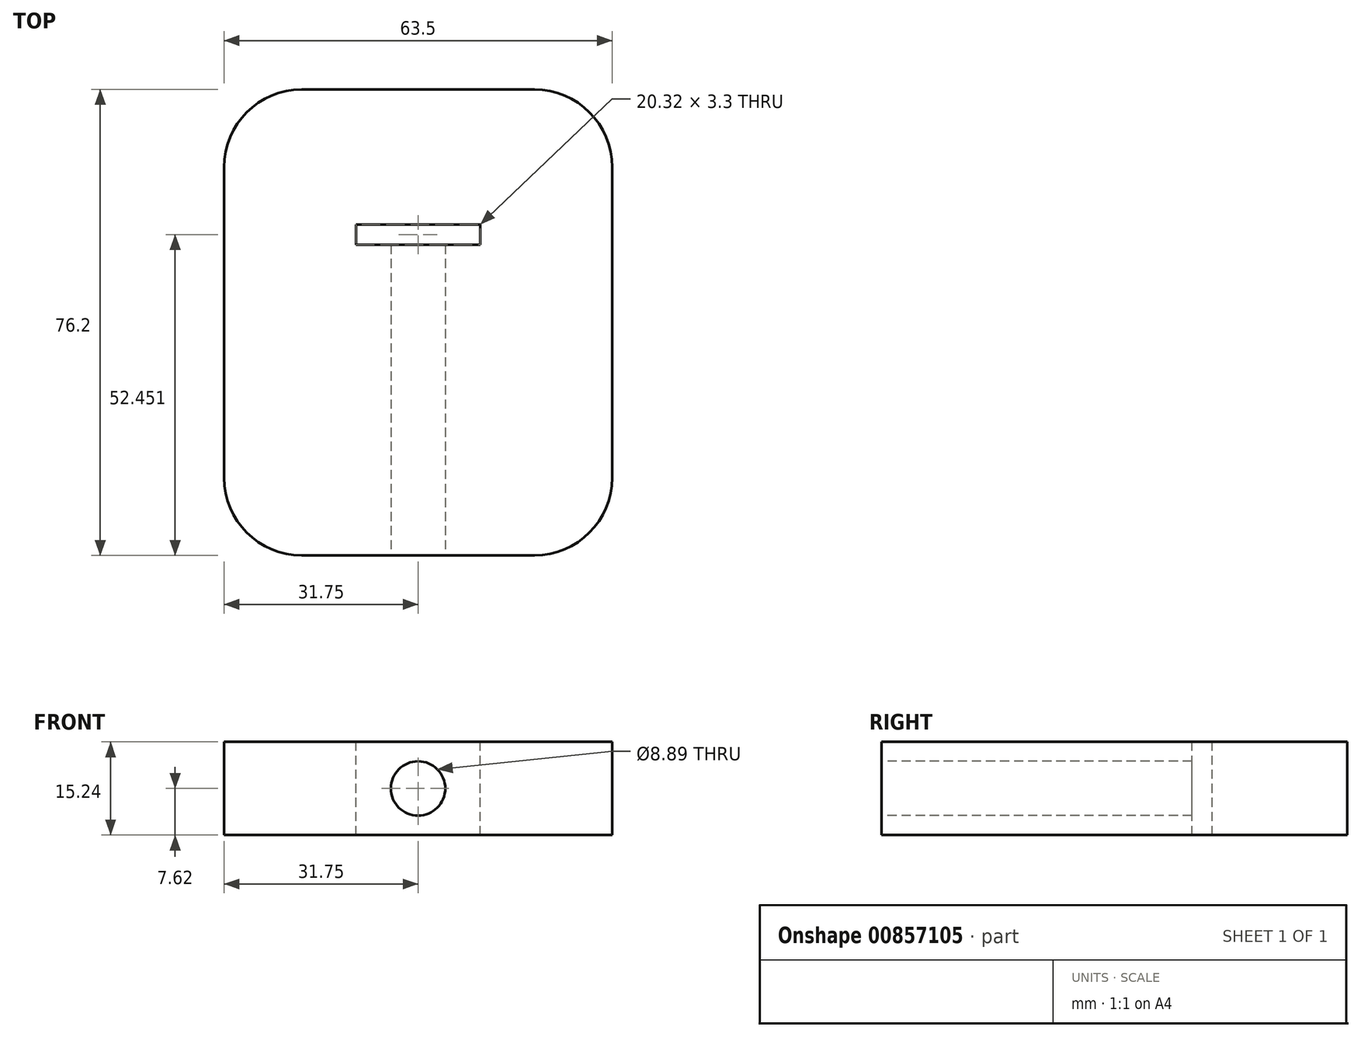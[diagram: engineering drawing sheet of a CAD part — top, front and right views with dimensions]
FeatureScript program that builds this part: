
annotation { "Feature Type Name" : "Feature", "Feature Type Description" : "" }
export const myFeature = defineFeature(function(context is Context, id is Id, definition is map)
    precondition{}
    {
        {
            var Q0;
            Q0=qCreatedBy(makeId("Top.planeOp"),FACE);
            var sketch = newSketch(context, id + "F0", { "sketchPlane" : qUnion([Q0])});
            skLineSegment(sketch, "E0.bottom", {"start": v(19.05, 38.1) * mm, "end": v(-19.05, 38.1) * mm});
            skLineSegment(sketch, "E0.top", {"start": v(19.05, -38.1) * mm, "end": v(-19.05, -38.1) * mm});
            skLineSegment(sketch, "E0.left", {"start": v(31.75, 25.4) * mm, "end": v(31.75, -25.4) * mm});
            skLineSegment(sketch, "E0.right", {"start": v(-31.75, 25.4) * mm, "end": v(-31.75, -25.4) * mm});
            skPoint(sketch, "E0.middle", {"position": v(0, 0) * mm});
            skPoint(sketch, "E1.visualSharp", {"position": v(-31.75, 38.1) * mm});
            skArc(sketch, "E1.filletArc", {"start": v(-19.05, 38.1) * mm, "mid": v(-28.03, 34.38) * mm, "end": v(-31.75, 25.4) * mm});
            skPoint(sketch, "E2.visualSharp", {"position": v(31.75, 38.1) * mm});
            skArc(sketch, "E2.filletArc", {"start": v(31.75, 25.4) * mm, "mid": v(28.03, 34.38) * mm, "end": v(19.05, 38.1) * mm});
            skPoint(sketch, "E3.visualSharp", {"position": v(31.75, -38.1) * mm});
            skArc(sketch, "E3.filletArc", {"start": v(19.05, -38.1) * mm, "mid": v(28.03, -34.38) * mm, "end": v(31.75, -25.4) * mm});
            skPoint(sketch, "E4.visualSharp", {"position": v(-31.75, -38.1) * mm});
            skArc(sketch, "E4.filletArc", {"start": v(-31.75, -25.4) * mm, "mid": v(-28.03, -34.38) * mm, "end": v(-19.05, -38.1) * mm});
            skSolve(sketch);
        }
        {
            var Q0;
            Q0=makeQuery(id+"F0.imprint","IMPRINT",FACE,{"disambiguationData":[TD([[makeQuery(id+"F0.imprint","IMPRINT",EDGE,{"derivedFrom":sQuery(id+"F0.wireOp",EDGE,"E0.bottom")}),1.0]])]});
            extrude(context, id + "F1", {"entities" : qUnion([Q0]), "depth" : 15.24 * mm, "offsetDistance" : 25.4 * mm});
        }
        {
            var Q0;
            Q0=makeQuery(id+"F1.opExtrude","SWEPT_FACE",FACE,{"disambiguationData":[OSD([sQuery(id+"F0.wireOp",EDGE,"E0.top")])]});
            var sketch = newSketch(context, id + "F2", { "sketchPlane" : qUnion([Q0])});
            skCircle(sketch, "E5", {"center": v(0, 7.62) * mm, "radius": 4.45 * mm});
            skSolve(sketch);
        }
        {
            var Q0;
            Q0 = qSketchRegion(id + "F2", true);
            var Q1;
            Q1=sQuery(id+"F2.wireOp",EDGE,"E5");
            extrude(context, id + "F3", {"entities" : qUnion([Q0]), "operationType" : NewBodyOperationType.REMOVE, "surfaceEntities" : qUnion([Q1]), "oppositeDirection" : true, "depth" : 50.8 * mm, "offsetDistance" : 25.4 * mm});
        }
        {
            var Q0;
            Q0=makeQuery(id+"F1.opExtrude","CAP_FACE",FACE,{"disambiguationData":[OSD([sQuery(id+"F0.wireOp",EDGE,"E0.bottom"),sQuery(id+"F0.wireOp",EDGE,"E0.top"),sQuery(id+"F0.wireOp",EDGE,"E0.left"),sQuery(id+"F0.wireOp",EDGE,"E0.right"),sQuery(id+"F0.wireOp",EDGE,"E1.filletArc"),sQuery(id+"F0.wireOp",EDGE,"E2.filletArc"),sQuery(id+"F0.wireOp",EDGE,"E3.filletArc"),sQuery(id+"F0.wireOp",EDGE,"E4.filletArc")])],"isStart":false});
            var sketch = newSketch(context, id + "F4", { "sketchPlane" : qUnion([Q0])});
            skLineSegment(sketch, "E6.bottom", {"start": v(-10.16, 16) * mm, "end": v(10.16, 16) * mm});
            skLineSegment(sketch, "E6.top", {"start": v(-10.16, 12.7) * mm, "end": v(10.16, 12.7) * mm});
            skLineSegment(sketch, "E6.left", {"start": v(-10.16, 16) * mm, "end": v(-10.16, 12.7) * mm});
            skLineSegment(sketch, "E6.right", {"start": v(10.16, 16) * mm, "end": v(10.16, 12.7) * mm});
            skSolve(sketch);
        }
        {
            var Q0;
            Q0=makeQuery(id+"F4.imprint","IMPRINT",FACE,{"disambiguationData":[TD([[makeQuery(id+"F4.imprint","IMPRINT",EDGE,{"derivedFrom":sQuery(id+"F4.wireOp",EDGE,"E6.bottom")}),-1.0]])]});
            extrude(context, id + "F5", {"entities" : qUnion([Q0]), "operationType" : NewBodyOperationType.REMOVE, "oppositeDirection" : true, "depth" : 15.24 * mm, "offsetDistance" : 25.4 * mm});
        }
    });
